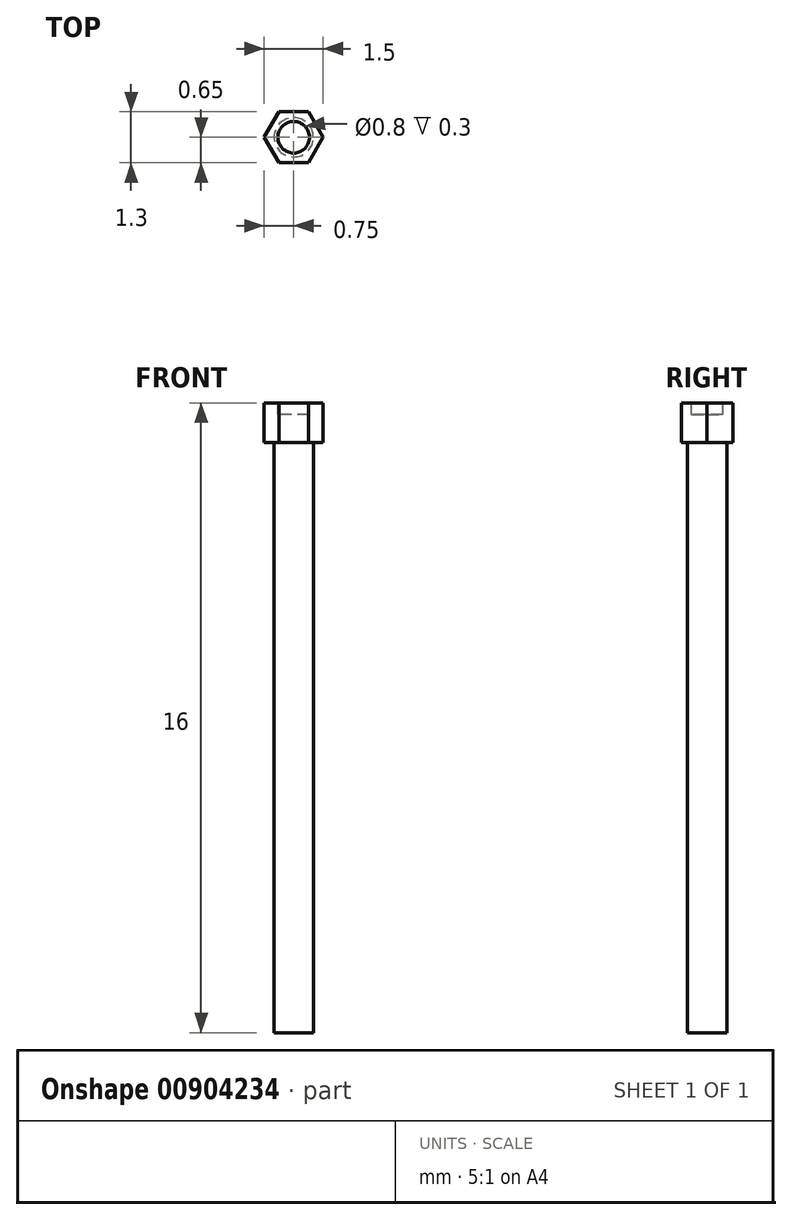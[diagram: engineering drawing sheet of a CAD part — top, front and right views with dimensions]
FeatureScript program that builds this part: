
annotation { "Feature Type Name" : "Feature", "Feature Type Description" : "" }
export const myFeature = defineFeature(function(context is Context, id is Id, definition is map)
    precondition{}
    {
        {
            var Q0;
            Q0=qCreatedBy(makeId("Front.planeOp"),FACE);
            var sketch = newSketch(context, id + "F0", { "sketchPlane" : qUnion([Q0])});
            skLineSegment(sketch, "E0.bottom", {"start": v(0, 0) * mm, "end": v(0.5, 0) * mm});
            skLineSegment(sketch, "E0.top", {"start": v(0, 15) * mm, "end": v(0.5, 15) * mm});
            skLineSegment(sketch, "E0.left", {"start": v(0, 0) * mm, "end": v(0, 15) * mm});
            skLineSegment(sketch, "E0.right", {"start": v(0.5, 0) * mm, "end": v(0.5, 15) * mm});
            skSolve(sketch);
        }
        {
            var Q0;
            Q0=makeQuery(id+"F0.imprint","IMPRINT",FACE,{"disambiguationData":[TD([[makeQuery(id+"F0.imprint","IMPRINT",EDGE,{"derivedFrom":sQuery(id+"F0.wireOp",EDGE,"E0.bottom")}),1.0]])]});
            var Q1;
            Q1=sQuery(id+"F0.wireOp",EDGE,"E0.left");
            revolve(context, id + "F1", {"surfaceOperationType" : NewSurfaceOperationType.NEW, "entities" : qUnion([Q0]), "axis" : qUnion([Q1]), "revolveType" : RevolveType.FULL});
        }
        {
            var Q0;
            Q0=makeQuery(id+"F1.opRevolve","SWEPT_FACE",FACE,{"disambiguationData":[OSD([sQuery(id+"F0.wireOp",EDGE,"E0.top")])]});
            var sketch = newSketch(context, id + "F2", { "sketchPlane" : qUnion([Q0])});
            skCircle(sketch, "E1.cCircle", {"center": v(0, 0) * mm, "radius": 0.75 * mm, "construction": true});
            skLineSegment(sketch, "E1.0", {"start": v(0.37, 0.65) * mm, "end": v(0.75, 0) * mm});
            skLineSegment(sketch, "E1.1", {"start": v(0.75, 0) * mm, "end": v(0.38, -0.65) * mm});
            skLineSegment(sketch, "E1.2", {"start": v(0.38, -0.65) * mm, "end": v(-0.37, -0.65) * mm});
            skLineSegment(sketch, "E1.3", {"start": v(-0.37, -0.65) * mm, "end": v(-0.75, 0) * mm});
            skLineSegment(sketch, "E1.4", {"start": v(-0.75, 0) * mm, "end": v(-0.38, 0.65) * mm});
            skLineSegment(sketch, "E1.5", {"start": v(-0.38, 0.65) * mm, "end": v(0.37, 0.65) * mm});
            skSolve(sketch);
        }
        {
            var Q0;
            Q0=makeQuery(id+"F2.imprint","IMPRINT",FACE,{"disambiguationData":[TD([[makeQuery(id+"F2.imprint","IMPRINT",EDGE,{"derivedFrom":makeQuery(id+"F1.opRevolve","SWEPT_EDGE",EDGE,{"disambiguationData":[OSD([sQuery(id+"F0.wireOp",EDGE,"E0.top"),sQuery(id+"F0.wireOp",EDGE,"E0.right")])]})}),-1.0]])]});
            var Q1;
            Q1=makeQuery(id+"F2.imprint","IMPRINT",FACE,{"disambiguationData":[TD([[makeQuery(id+"F2.imprint","IMPRINT",EDGE,{"derivedFrom":sQuery(id+"F2.wireOp",EDGE,"E1.0")}),-1.0]])]});
            extrude(context, id + "F3", {"entities" : qUnion([Q0, Q1]), "operationType" : NewBodyOperationType.ADD, "depth" : 1 * mm, "offsetDistance" : 25 * mm});
        }
        {
            var Q0;
            Q0=makeQuery(id+"F3.opExtrude","CAP_FACE",FACE,{"disambiguationData":[OSD([sQuery(id+"F2.wireOp",EDGE,"E1.0"),sQuery(id+"F2.wireOp",EDGE,"E1.1"),sQuery(id+"F2.wireOp",EDGE,"E1.2"),sQuery(id+"F2.wireOp",EDGE,"E1.3"),sQuery(id+"F2.wireOp",EDGE,"E1.4"),sQuery(id+"F2.wireOp",EDGE,"E1.5")])],"isStart":false});
            var sketch = newSketch(context, id + "F4", { "sketchPlane" : qUnion([Q0])});
            skCircle(sketch, "E2", {"center": v(0, 0) * mm, "radius": 0.4 * mm});
            skSolve(sketch);
        }
        {
            var Q0;
            Q0=makeQuery(id+"F4.imprint","IMPRINT",FACE,{"disambiguationData":[TD([[makeQuery(id+"F4.imprint","IMPRINT",EDGE,{"derivedFrom":sQuery(id+"F4.wireOp",EDGE,"E2")}),1.0]])]});
            extrude(context, id + "F5", {"entities" : qUnion([Q0]), "operationType" : NewBodyOperationType.REMOVE, "oppositeDirection" : true, "depth" : 0.3 * mm, "offsetDistance" : 25 * mm});
        }
    });
